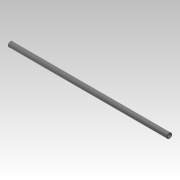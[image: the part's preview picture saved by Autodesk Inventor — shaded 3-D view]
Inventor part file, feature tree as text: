
AUTODESK INVENTOR PART (.ipt)
format: ipt  version: 2020 (Build 240168000, 168)  size: 87,040 bytes
history: native  units: mm
features: revolve x1, chamfer x1, sketch x1
ambient origin geometry x8: Origin, YZ Plane, XZ Plane, XY Plane, X Axis, Y Axis, Z Axis, Center Point
bodies: Solid1 (feature_tree)
feature tree (3):
  revolve  "Revolution1"  [1 undecoded]
  chamfer  "Chamfer1"  Distance=250.0mm
  sketch  "Sketch1"  dims[d0=3.0mm d1=4.0mm d2=250.0mm d3=90.0deg d4=0.5mm d5=2.0mm d6=45.0deg]
note: 1 required parameter value undecoded (feature->parameter linkage not recoverable at this tier; creation-order binding heuristic only, values carry confidence <= 0.55)
